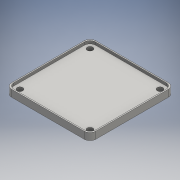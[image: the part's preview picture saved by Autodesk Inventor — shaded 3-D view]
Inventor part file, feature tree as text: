
AUTODESK INVENTOR PART (.ipt)
format: ipt  version: 2016 (Build 200138000, 138)  size: 153,600 bytes
history: native  units: mm
features: sketch x3, extrude x2, hole x1
ambient origin geometry x8: Origin, YZ Plane, XZ Plane, XY Plane, X Axis, Y Axis, Z Axis, Center Point
bodies: Body1 (feature_tree)
feature tree (6):
  extrude  "Extrusion3"  Depth=150.0mm
  hole  "Hole3"  [1 undecoded]
  extrude  "Extrusion4"  Depth=7.5mm TaperAngle=0.0deg
  sketch  "Sketch5"  dims[d36=150.0mm d37=150.0mm]
  sketch  "Sketch6"  dims[d38=75.0mm d39=75.0mm]
  sketch  "Sketch7"  dims[d40=10.0mm d41=7.5mm d42=0.0mm d43=125.0mm d44=125.0mm d45=62.5mm d46=62.5mm d47=6.6mm d48=6.0mm d49=10.0mm d50=6.5mm d51=90.0deg d52=8.0mm d53=20.594885mm d54=2.0mm d55=2.0mm d56=2.0mm d57=2.0mm d58=10.0mm d59=10.0mm d60=10.0mm d61=10.0mm d62=5.0mm d63=0.0mm]
note: 1 required parameter value undecoded (feature->parameter linkage not recoverable at this tier; creation-order binding heuristic only, values carry confidence <= 0.55)
